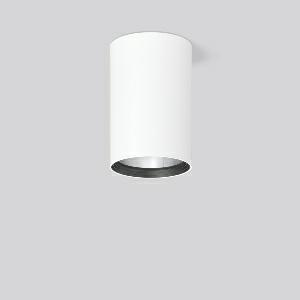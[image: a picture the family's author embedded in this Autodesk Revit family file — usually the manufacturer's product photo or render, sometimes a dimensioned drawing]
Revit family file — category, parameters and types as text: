
# Revit family: heledon_maxi_a_931223_002_3_5994
name_source: partatom
category: Lighting Fixtures
units: mm (PartAtom-declared; Revit-internal decimal feet)

## family parameters
Cut with Voids When Loaded = No
Host = Face
Light Source = No
Part Type = Normal
Room Calculation Point = No
Round Connector Dimension = Use Diameter
Shared = No

## types (1)
- HELEDON maxi A (1 x LED Modul 935, 4250 lm, 3500)
    Apparent Load = 35 VA
    Approval mark = CE
    CIE Flux Codes = 100 100 100 100 100
    Color Rendering = 92
    Color Temperature = 3500
    Default Elevation = 1800 mm
    Description = Series: HELEDON maxi
Cylindrical surface-mounted downlight. Housing: die-cast aluminium, powder-coated. Internal ceiling frame polycarbonate with bayonet mounting. Black plastic ring and recessed LED to prevent glare from the side. Optical assembly with reflector made of MIRO-Silver with 98% total light reflection for outstanding efficiency - can be changed without tools. Best colour rendering index Ra>90. Suitable for Ceiling mounting. Easy installation with a separate ceiling frame with bayonet mounting and plug connection. Driver integrated. Connected via plug-in connector. High quality converter without flickering and stroboscopic effect. The following accessories can be mounted without use of tools: interchangeable lenses, decorative glasses, honeycomb louvre, clear and frosted diffusers, white interchangeable plastic ring. 
Colour: traffic white, matt (RAL 9016)
Diameter: 123 mm
Height: 183 mm
Lamp: LED
Socket: without socket
Colour temperature: 3500K
Colour rendering index (CRI): 92
System power: 35 W
Rated luminous flux: 4250 lm
Luminous efficiency: 121 lm/W
Control gear: Regulated power supply
Protection class: I
Type of protection: IP 20
    Height = 183 mm
    Lamp = 1 x LED Modul 935
    Lamp Light Flux = 4250 lm
    Lamp count = 1
    Length = 123 mm
    Lifetime = 50000 h
    Luminous efficacy = 121 lm/W
    Manufacturer = RZB
    ModVariant = No
    Model = 931223.002.3
    Mounting Place = Ceiling
    Mounting Type = Surface mounted
    Number of Poles = 1
    OnlyDefault = Yes
    Power Factor = 1
    Product Name = HELEDON maxi A
    Product group = Surface mounted downlights
    ProductGroupID = 302
    Protection Class = Protection class I
    Protection Degree = IP 20
    RLX_Detail_Level = 1
    RLX_Emergency_Light_Flux = 0 lm
    RLX_Emergency_Type = 0
    RLX_Emergency_Type_DB = No
    RlxData = <blob elided: 97053 chars, md5=c298fa36>
    Socket = socket
    Standby Power = 0 W
    System Light Flux = 4250 lm
    System Power = 35 W
    Type Comments = Product without accessories
    Type Image = 931192.002.jpg
    URL = http://relux.com
    VarID = ---
    Voltage = 230 V
    Voltage Range = 220-240 V
    Weight = 0.00 kg
    Width = 0 mm  [stored 0 ft]

note: [stored X ft] marks values corroborated as IEEE doubles in the binary element streams (Revit-internal decimal feet)

## geometry (parser evidence)
native form markers: Blend x4, Sweep x9
no freeform markers — native parametric forms only
